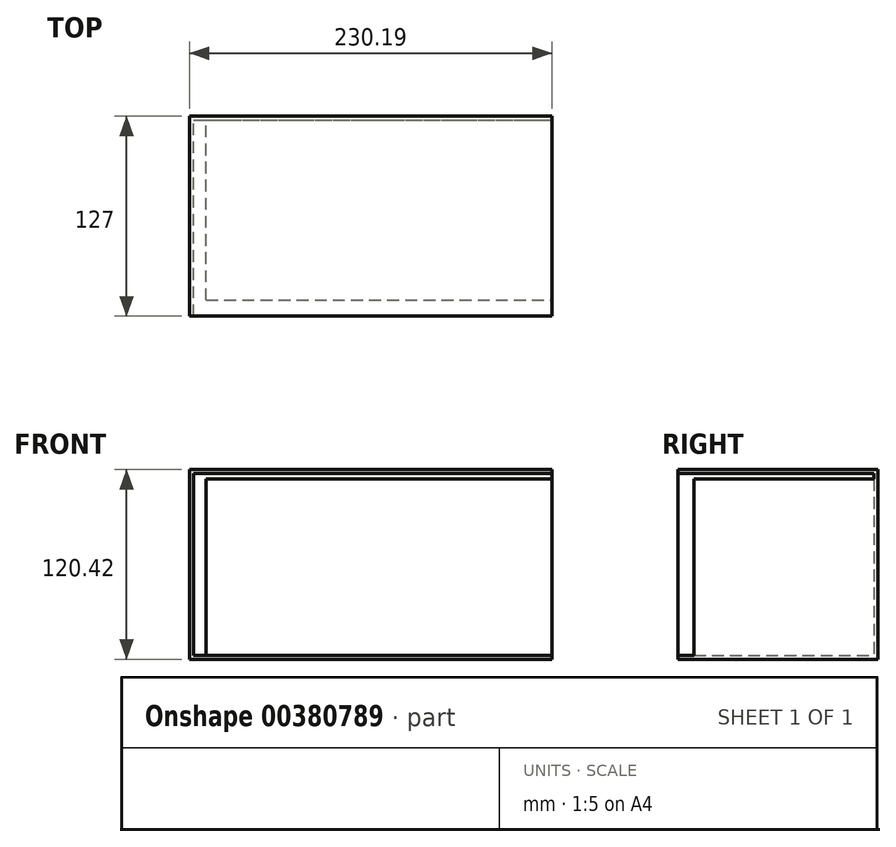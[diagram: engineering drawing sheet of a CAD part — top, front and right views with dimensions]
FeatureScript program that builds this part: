
annotation { "Feature Type Name" : "Feature", "Feature Type Description" : "" }
export const myFeature = defineFeature(function(context is Context, id is Id, definition is map)
    precondition{}
    {
        {
            var Q0;
            Q0=qCreatedBy(makeId("Front.planeOp"),FACE);
            var sketch = newSketch(context, id + "F0", { "sketchPlane" : qUnion([Q0])});
            skLineSegment(sketch, "E0.bottom", {"start": v(-153.98, 43.68) * mm, "end": v(76.2, 43.68) * mm});
            skLineSegment(sketch, "E0.top", {"start": v(-153.98, -76.74) * mm, "end": v(76.2, -76.74) * mm});
            skLineSegment(sketch, "E0.left", {"start": v(-153.98, 43.68) * mm, "end": v(-153.98, -76.74) * mm});
            skLineSegment(sketch, "E0.right", {"start": v(76.2, 43.68) * mm, "end": v(76.2, -76.74) * mm});
            skLineSegment(sketch, "E1", {"start": v(76.2, 16.94) * mm, "end": v(-38.02, 16.94) * mm});
            skLineSegment(sketch, "E2", {"start": v(-38.02, 16.94) * mm, "end": v(-135.63, -73.06) * mm});
            skLineSegment(sketch, "E3", {"start": v(-135.63, -73.06) * mm, "end": v(76.2, -73.06) * mm});
            skLineSegment(sketch, "E4", {"start": v(76.2, 16.94) * mm, "end": v(76.2, -73.06) * mm});
            skLineSegment(sketch, "E5", {"start": v(-38.02, 16.94) * mm, "end": v(27.77, 77.6) * mm});
            skSolve(sketch);
        }
        {
            var Q0;
            {var subQ1=sQuery(id+"F0.wireOp",EDGE,"E0.top");Q0=makeQuery(id+"F0.imprint","IMPRINT",FACE,{"disambiguationData":[TD([[makeQuery(id+"F0.imprint","IMPRINT",EDGE,{"derivedFrom":subQ1}),1.0]])]});}
            var Q1;
            {var subQ5=sQuery(id+"F0.wireOp",EDGE,"E1");Q1=makeQuery(id+"F0.imprint","IMPRINT",FACE,{"disambiguationData":[TD([[makeQuery(id+"F0.imprint","IMPRINT",EDGE,{"derivedFrom":subQ5}),-1.0]])]});}
            var Q2;
            Q2=makeQuery(id+"F0.imprint","IMPRINT",FACE,{"disambiguationData":[TD([[makeQuery(id+"F0.imprint","IMPRINT",EDGE,{"derivedFrom":sQuery(id+"F0.wireOp",EDGE,"E1")}),1.0]])]});
            extrude(context, id + "F1", {"entities" : qUnion([Q0, Q1, Q2]), "depth" : 127 * mm});
        }
        {
            var Q0;
            Q0=makeQuery(id+"F1.opExtrude","CAP_FACE",FACE,{"disambiguationData":[OSD([sQuery(id+"F0.wireOp",EDGE,"E0.bottom"),sQuery(id+"F0.wireOp",EDGE,"E0.top"),sQuery(id+"F0.wireOp",EDGE,"E0.left"),sQuery(id+"F0.wireOp",EDGE,"E0.right"),sQuery(id+"F0.wireOp",EDGE,"E4")])],"isStart":false});
            var Q1;
            Q1=makeQuery(id+"F1.opExtrude","SWEPT_FACE",FACE,{"disambiguationData":[OSD([sQuery(id+"F0.wireOp",EDGE,"E0.right"),sQuery(id+"F0.wireOp",EDGE,"E4")])]});
            shell(context, id + "F2", {"entities" : qUnion([Q0, Q1]), "thickness" : 2.54 * mm});
        }
        {
            var Q0;
            Q0=makeQuery(id+"F2.opShell","OFFSET_FACE",FACE,{"disambiguationData":[OSD([sQuery(id+"F0.wireOp",EDGE,"E0.bottom"),sQuery(id+"F0.wireOp",EDGE,"E0.top"),sQuery(id+"F0.wireOp",EDGE,"E0.left"),sQuery(id+"F0.wireOp",EDGE,"E0.right"),sQuery(id+"F0.wireOp",EDGE,"E4")])]});
            var sketch = newSketch(context, id + "F3", { "sketchPlane" : qUnion([Q0])});
            skLineSegment(sketch, "E6.bottom", {"start": v(-143.4, 37.76) * mm, "end": v(87.37, 37.76) * mm});
            skLineSegment(sketch, "E6.top", {"start": v(-143.4, -74.2) * mm, "end": v(87.37, -74.2) * mm});
            skLineSegment(sketch, "E6.left", {"start": v(-143.4, 37.76) * mm, "end": v(-143.4, -74.2) * mm});
            skLineSegment(sketch, "E6.right", {"start": v(87.37, 37.76) * mm, "end": v(87.37, -74.2) * mm});
            skSolve(sketch);
        }
        {
            var Q0;
            {var subQ0=sQuery(id+"F3.wireOp",EDGE,"E6.left");Q0=makeQuery(id+"F3.imprint","IMPRINT",FACE,{"disambiguationData":[TD([[makeQuery(id+"F3.imprint","IMPRINT",EDGE,{"derivedFrom":subQ0}),1.0]])]});}
            extrude(context, id + "F4", {"entities" : qUnion([Q0]), "operationType" : NewBodyOperationType.ADD, "depth" : 114.3 * mm});
        }
    });
